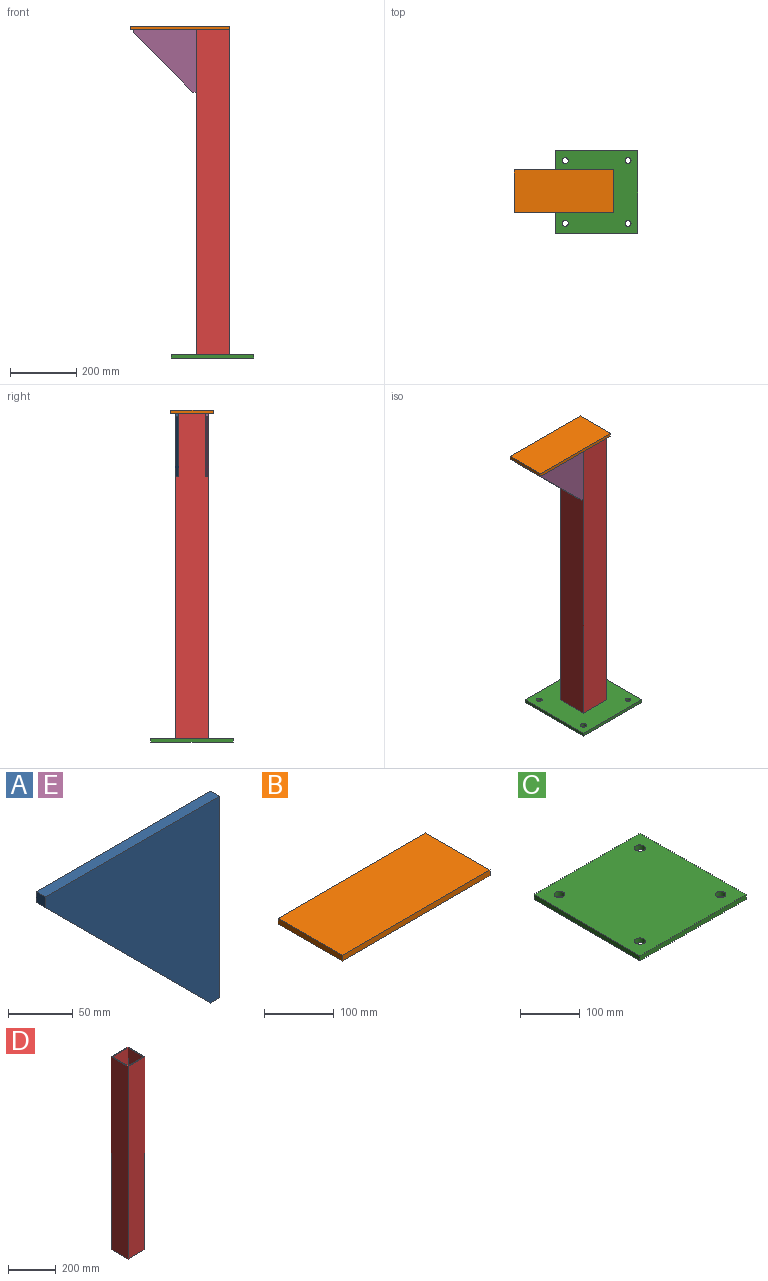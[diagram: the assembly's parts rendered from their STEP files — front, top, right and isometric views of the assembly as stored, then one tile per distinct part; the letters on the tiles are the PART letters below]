
ASSEMBLY  parts=5 mates=4
PART A: 7 faces, bbox 190x10x190 mm
  f0: plane 10x10mm, normal (-1,0,0), area 100mm2, adj f1,f4,f5,f6
  f1: plane 180x180mm, normal (-0.71,0,-0.71), area 2545.6mm2, adj f0,f2,f5,f6
  f2: plane 10x10mm, normal (0,0,-1), area 100mm2, adj f1,f3,f5,f6
  f3: plane 190x10mm, normal (1,0,0), area 1900mm2, adj f2,f4,f5,f6
  f4: plane 190x10mm, normal (0,0,1), area 1900mm2, adj f0,f3,f5,f6
  f5: plane 190x190mm, normal (0,-1,0), area 19900mm2, adj f0,f1,f2,f3,f4
  f6: plane 190x190mm, normal (0,1,0), area 19900mm2, adj f0,f1,f2,f3,f4
PART B: 6 faces, bbox 300x130x10 mm
  f0: plane 300x10mm, normal (0,-1,0), area 3000mm2, adj f1,f3,f4,f5
  f1: plane 130x10mm, normal (1,0,0), area 1300mm2, adj f0,f2,f4,f5
  f2: plane 300x10mm, normal (0,1,0), area 3000mm2, adj f1,f3,f4,f5
  f3: plane 130x10mm, normal (-1,0,0), area 1300mm2, adj f0,f2,f4,f5
  f4: plane 300x130mm, normal (0,0,1), area 39000mm2, adj f0,f1,f2,f3
  f5: plane 300x130mm, normal (0,0,-1), area 39000mm2, adj f0,f1,f2,f3
PART C: 10 faces, bbox 250x250x10 mm
  f0: plane 250x10mm, normal (0,-1,0), area 2500mm2, adj f1,f7,f8,f9
  f1: plane 250x10mm, normal (1,0,0), area 2500mm2, adj f0,f2,f8,f9
  f2: plane 250x10mm, normal (0,1,0), area 2500mm2, adj f1,f7,f8,f9
  f3: cylinder r=9mm len=18mm, axis (0,0,-1), area 565.5mm2, adj f8,f9
  f4: cylinder r=9mm len=18mm, axis (0,0,-1), area 565.5mm2, adj f8,f9
  f5: cylinder r=9mm len=18mm, axis (0,0,-1), area 565.5mm2, adj f8,f9
  f6: cylinder r=9mm len=18mm, axis (0,0,-1), area 565.5mm2, adj f8,f9
  f7: plane 250x10mm, normal (-1,0,0), area 2500mm2, adj f0,f2,f8,f9
  f8: plane 250x250mm, normal (0,0,1), area 61482.1mm2, adj f0,f1,f2,f3,f4,f5,f6,f7
  f9: plane 250x250mm, normal (0,0,-1), area 61482.1mm2, adj f0,f1,f2,f3,f4,f5,f6,f7
PART D: 10 faces, bbox 100x100x985 mm
  f0: plane 985x100mm, normal (0,-1,0), area 98500mm2, adj f1,f7,f8,f9
  f1: plane 985x100mm, normal (1,0,0), area 98500mm2, adj f0,f2,f8,f9
  f2: plane 985x100mm, normal (0,1,0), area 98500mm2, adj f1,f7,f8,f9
  f3: plane 985x90mm, normal (-1,0,0), area 88650mm2, adj f4,f6,f8,f9
  f4: plane 985x90mm, normal (0,1,0), area 88650mm2, adj f3,f5,f8,f9
  f5: plane 985x90mm, normal (1,0,0), area 88650mm2, adj f4,f6,f8,f9
  f6: plane 985x90mm, normal (0,-1,0), area 88650mm2, adj f3,f5,f8,f9
  f7: plane 985x100mm, normal (-1,0,0), area 98500mm2, adj f0,f2,f8,f9
  f8: plane 100x100mm, normal (0,0,1), area 1900mm2, adj f0,f1,f2,f3,f4,f5,f6,f7
  f9: plane 100x100mm, normal (0,0,-1), area 1900mm2, adj f0,f1,f2,f3,f4,f5,f6,f7
PART E: same geometry as A
PLACE A t=(-115.92,69.16,886.05)mm
PLACE B t=(-70.92,19.16,981.05)mm
PLACE C t=(29.08,19.16,-13.95)mm
PLACE D t=(29.08,19.16,-3.95)mm
PLACE E t=(-115.92,-20.84,886.05)mm
MATE fastened E.f3 <-> D.f7  axis (1,0,0) through (-20.92,-30.84,981.05)mm
MATE fastened B.f5 <-> D.f8  axis (0,0,-1) through (79.08,19.16,981.05)mm
MATE fastened A.f3 <-> D.f7  axis (1,0,0) through (-20.92,69.16,981.05)mm
MATE fastened C.f8 <-> D.f9  axis (0,0,1) through (29.08,19.16,-3.95)mm
